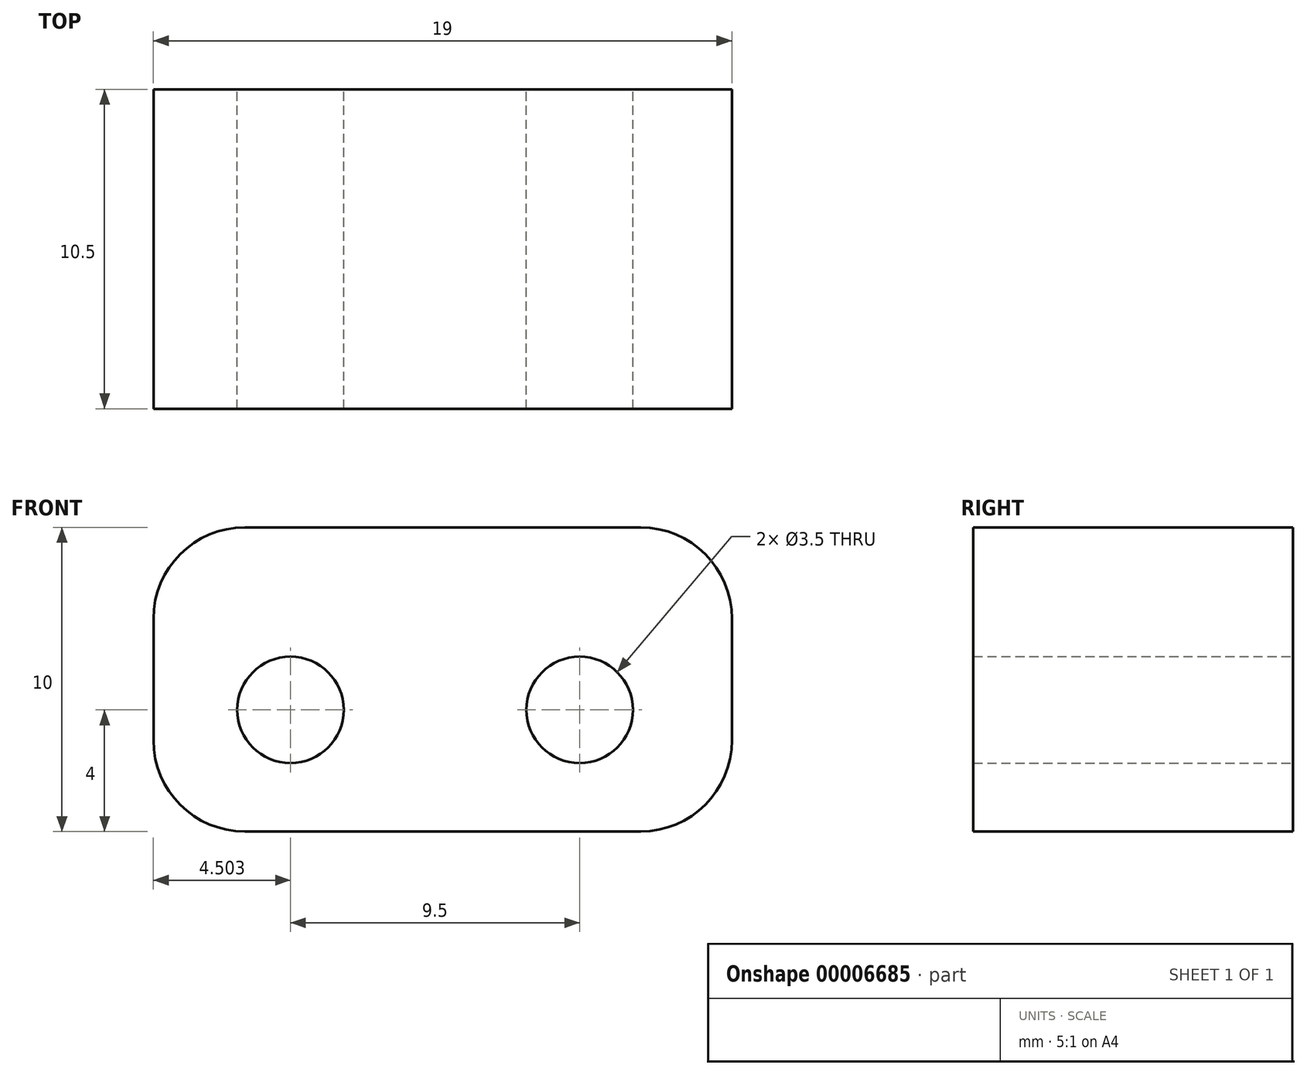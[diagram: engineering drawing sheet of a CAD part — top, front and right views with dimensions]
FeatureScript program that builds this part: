
annotation { "Feature Type Name" : "Feature", "Feature Type Description" : "" }
export const myFeature = defineFeature(function(context is Context, id is Id, definition is map)
    precondition{}
    {
        {
            var Q0;
            Q0=qCreatedBy(makeId("Front.planeOp"),FACE);
            var sketch = newSketch(context, id + "F0", { "sketchPlane" : qUnion([Q0])});
            skLineSegment(sketch, "E0.bottom", {"start": v(4.33, 0) * mm, "end": v(17.33, 0) * mm});
            skLineSegment(sketch, "E0.top", {"start": v(4.33, 10) * mm, "end": v(17.33, 10) * mm});
            skLineSegment(sketch, "E0.left", {"start": v(1.33, 3) * mm, "end": v(1.33, 7) * mm});
            skLineSegment(sketch, "E0.right", {"start": v(20.33, 3) * mm, "end": v(20.33, 7) * mm});
            skCircle(sketch, "E1", {"center": v(5.83, 4) * mm, "radius": 1.75 * mm});
            skCircle(sketch, "E2", {"center": v(15.33, 4) * mm, "radius": 1.75 * mm});
            skPoint(sketch, "E3.visualSharp", {"position": v(1.33, 10) * mm});
            skArc(sketch, "E3.filletArc", {"start": v(4.33, 10) * mm, "mid": v(2.21, 9.12) * mm, "end": v(1.33, 7) * mm});
            skPoint(sketch, "E4.visualSharp", {"position": v(20.33, 10) * mm});
            skArc(sketch, "E4.filletArc", {"start": v(20.33, 7) * mm, "mid": v(19.45, 9.12) * mm, "end": v(17.33, 10) * mm});
            skPoint(sketch, "E5.visualSharp", {"position": v(20.33, 0) * mm});
            skArc(sketch, "E5.filletArc", {"start": v(17.33, 0) * mm, "mid": v(19.45, 0.88) * mm, "end": v(20.33, 3) * mm});
            skPoint(sketch, "E6.visualSharp", {"position": v(1.33, 0) * mm});
            skArc(sketch, "E6.filletArc", {"start": v(1.33, 3) * mm, "mid": v(2.21, 0.88) * mm, "end": v(4.33, 0) * mm});
            skSolve(sketch);
        }
        {
            var Q0;
            Q0 = qSketchRegion(id + "F0", true);
            extrude(context, id + "F1", {"entities" : qUnion([Q0]), "depth" : 10.5 * mm});
        }
    });
